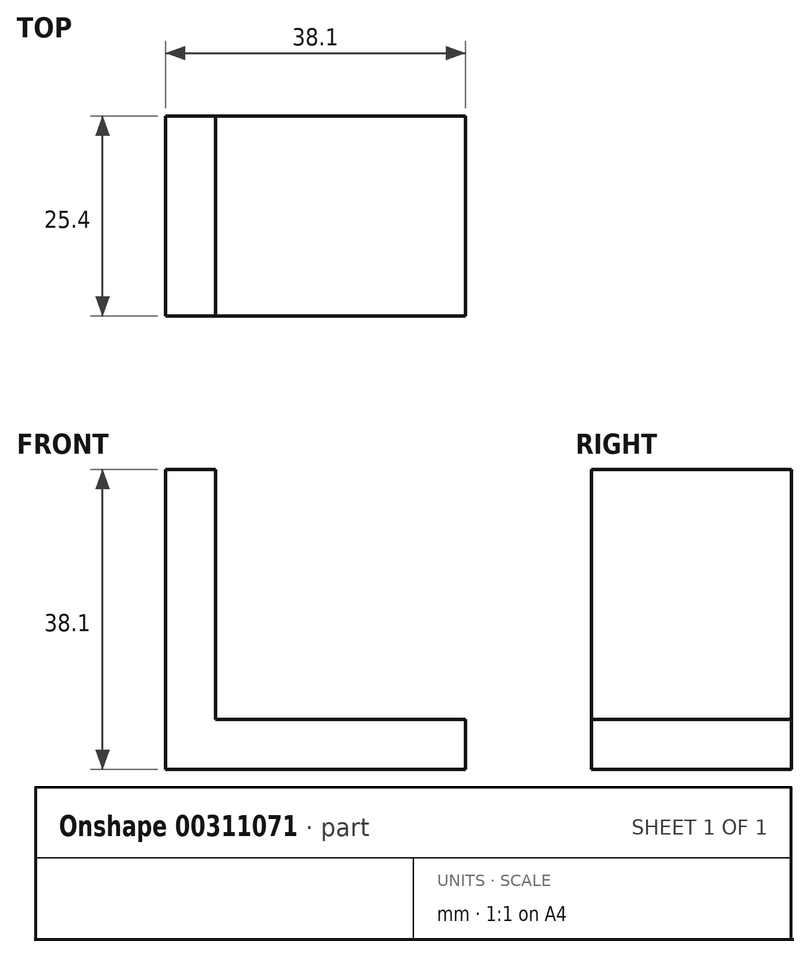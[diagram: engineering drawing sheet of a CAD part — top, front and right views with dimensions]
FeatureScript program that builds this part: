
annotation { "Feature Type Name" : "Feature", "Feature Type Description" : "" }
export const myFeature = defineFeature(function(context is Context, id is Id, definition is map)
    precondition{}
    {
        {
            var Q0;
            Q0=qCreatedBy(makeId("Front.planeOp"),FACE);
            var sketch = newSketch(context, id + "F0", { "sketchPlane" : qUnion([Q0])});
            skLineSegment(sketch, "E0", {"start": v(0, 0) * mm, "end": v(0, 38.1) * mm});
            skLineSegment(sketch, "E1", {"start": v(0, 38.1) * mm, "end": v(6.35, 38.1) * mm});
            skLineSegment(sketch, "E2", {"start": v(6.35, 38.1) * mm, "end": v(6.35, 6.35) * mm});
            skLineSegment(sketch, "E3", {"start": v(6.35, 6.35) * mm, "end": v(38.1, 6.35) * mm});
            skLineSegment(sketch, "E4", {"start": v(38.1, 6.35) * mm, "end": v(38.1, 0) * mm});
            skLineSegment(sketch, "E5", {"start": v(38.1, 0) * mm, "end": v(0, 0) * mm});
            skSolve(sketch);
        }
        {
            var Q0;
            Q0 = qSketchRegion(id + "F0", true);
            extrude(context, id + "F1", {"entities" : qUnion([Q0]), "depth" : 25.4 * mm});
        }
    });
